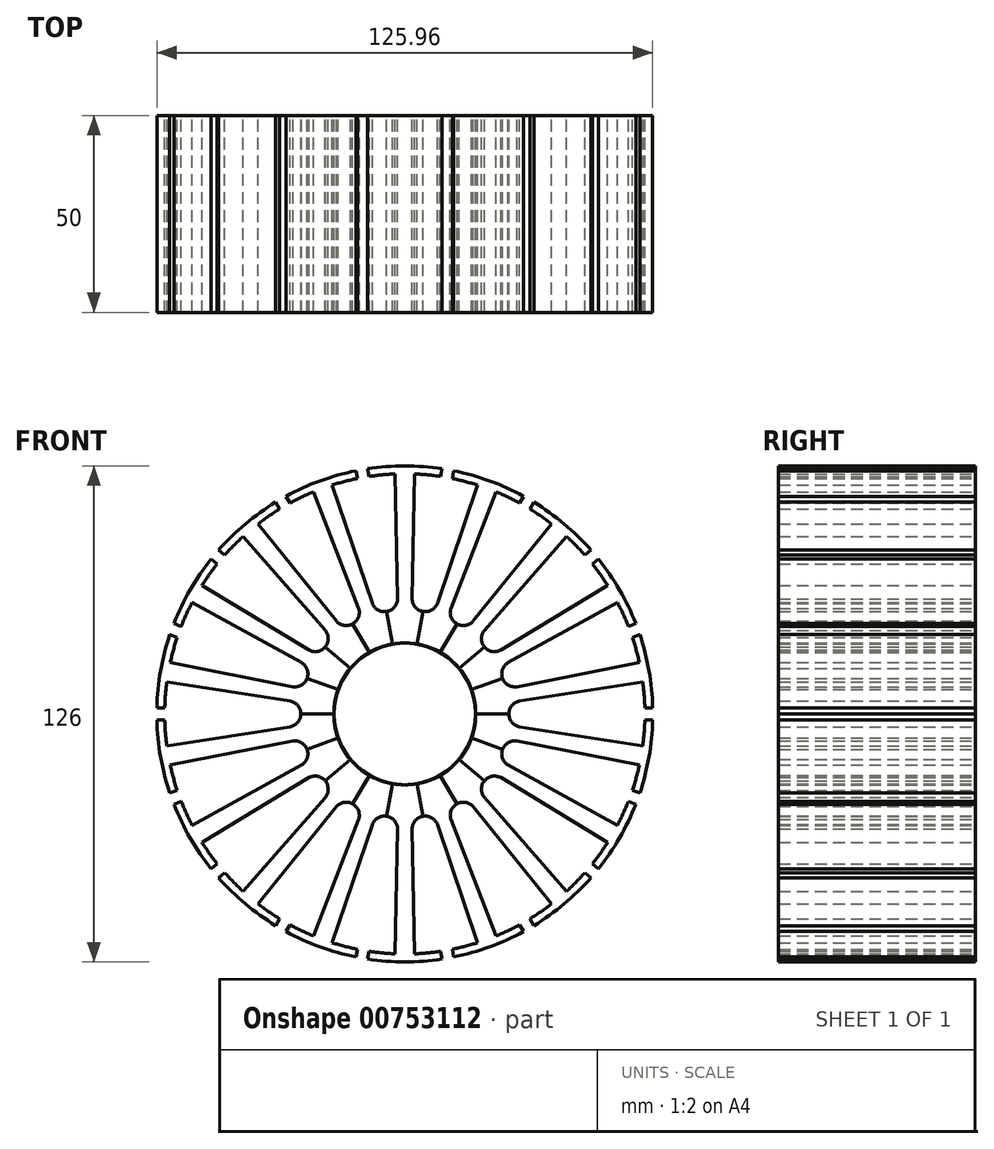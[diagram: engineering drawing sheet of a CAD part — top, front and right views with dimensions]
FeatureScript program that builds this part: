
annotation { "Feature Type Name" : "Feature", "Feature Type Description" : "" }
export const myFeature = defineFeature(function(context is Context, id is Id, definition is map)
    precondition{}
    {
        {
            var Q0;
            Q0=qCreatedBy(makeId("Front.planeOp"),FACE);
            var sketch = newSketch(context, id + "F0", { "sketchPlane" : qUnion([Q0])});
            skLineSegment(sketch, "E0", {"start": v(1.84, 29.2) * mm, "end": v(1.85, 29.2) * mm});
            skCircle(sketch, "E1", {"center": v(0, 0) * mm, "radius": 18 * mm});
            skPoint(sketch, "E2.startSnap0", {"position": v(0, 63) * mm});
            skLineSegment(sketch, "E3", {"start": v(0, 63) * mm, "end": v(0, 0) * mm});
            skLineSegment(sketch, "E4", {"start": v(1.84, 29.2) * mm, "end": v(2.48, 60.97) * mm});
            skLineSegment(sketch, "E5.MirrorCS", {"start": v(9.11, 60.32) * mm, "end": v(9.46, 62.29) * mm});
            skPoint(sketch, "E6.MirrorCS.end.orphan", {"position": v(9.11, 60.32) * mm});
            skArc(sketch, "E7", {"start": v(-9.46, 62.29) * mm, "mid": v(0, 63) * mm, "end": v(9.46, 62.29) * mm});
            skArc(sketch, "E8.trimOffspring", {"start": v(2.48, 60.95) * mm, "mid": v(5.8, 60.72) * mm, "end": v(9.11, 60.32) * mm});
            skArc(sketch, "E9.MirrorCS", {"start": v(30.2, 55.3) * mm, "mid": v(21.55, 59.2) * mm, "end": v(12.41, 61.76) * mm});
            skLineSegment(sketch, "E10.MirrorCS", {"start": v(12.07, 59.8) * mm, "end": v(12.41, 61.76) * mm});
            skArc(sketch, "E11.MirrorCS", {"start": v(18.52, 58.12) * mm, "mid": v(15.31, 59.05) * mm, "end": v(12.07, 59.8) * mm});
            skLineSegment(sketch, "E12.MirrorCS", {"start": v(8.26, 28.08) * mm, "end": v(18.52, 58.14) * mm});
            skLineSegment(sketch, "E13.MirrorCS", {"start": v(29.2, 53.56) * mm, "end": v(30.2, 55.3) * mm});
            skArc(sketch, "E14.MirrorCS", {"start": v(29.2, 53.56) * mm, "mid": v(26.23, 55.07) * mm, "end": v(23.18, 56.42) * mm});
            skLineSegment(sketch, "E15.MirrorCS", {"start": v(23.19, 56.44) * mm, "end": v(11.72, 26.82) * mm});
            skArc(sketch, "E16", {"start": v(1.84, 29.2) * mm, "mid": v(4.59, 26.02) * mm, "end": v(8.26, 28.08) * mm});
            skArc(sketch, "E17.MirrorCS", {"start": v(17.37, 23.56) * mm, "mid": v(13.21, 22.88) * mm, "end": v(11.72, 26.82) * mm});
            skLineSegment(sketch, "E18", {"start": v(5.17, 29.3) * mm, "end": v(0, 0) * mm});
            skLineSegment(sketch, "E19.MirrorCS", {"start": v(-9.11, 60.32) * mm, "end": v(-9.46, 62.29) * mm});
            skLineSegment(sketch, "E20.MirrorCS", {"start": v(-1.84, 29.2) * mm, "end": v(-2.48, 60.97) * mm});
            skArc(sketch, "E21.MirrorCS", {"start": v(-2.48, 60.95) * mm, "mid": v(-5.8, 60.72) * mm, "end": v(-9.11, 60.32) * mm});
            skLineSegment(sketch, "E22.MirrorCS", {"start": v(-5.17, 29.3) * mm, "end": v(0, 0) * mm});
            skArc(sketch, "E23.MirrorCS", {"start": v(-1.84, 29.2) * mm, "mid": v(-4.59, 26.02) * mm, "end": v(-8.26, 28.08) * mm});
            skSolve(sketch);
        }
        {
            var Q0;
            Q0=qSketchRegion(id+"F0",true);
            extrude(context, id + "F1", {"entities" : qUnion([Q0]), "depth" : 50 * mm, "offsetDistance" : 25 * mm});
        }
        {
            var Q0;
            Q0=makeQuery(id+"F1.opExtrude","SWEPT_BODY",BODY,{"disambiguationData":[OSD([sQuery(id+"F0.wireOp",EDGE,"E1"),sQuery(id+"F0.wireOp",EDGE,"E5.MirrorCS"),sQuery(id+"F0.wireOp",EDGE,"E7"),sQuery(id+"F0.wireOp",EDGE,"E8.trimOffspring"),sQuery(id+"F0.wireOp",EDGE,"E16"),sQuery(id+"F0.wireOp",EDGE,"E4"),sQuery(id+"F0.wireOp",EDGE,"E18"),sQuery(id+"F0.wireOp",EDGE,"E20.MirrorCS"),sQuery(id+"F0.wireOp",EDGE,"E21.MirrorCS"),sQuery(id+"F0.wireOp",EDGE,"E19.MirrorCS"),sQuery(id+"F0.wireOp",EDGE,"E22.MirrorCS"),sQuery(id+"F0.wireOp",EDGE,"E23.MirrorCS")])]});
            var Q1;
            Q1=makeQuery(id+"F1.opExtrude","SWEPT_FACE",FACE,{"disambiguationData":[OSD([sQuery(id+"F0.wireOp",EDGE,"E1")])]});
            circularPattern(context, id + "F2", {"entities" : qUnion([Q0]), "axis" : qUnion([Q1]), "angle" : 360 * degree, "instanceCount" : 18, "equalSpace" : true});
        }
    });
